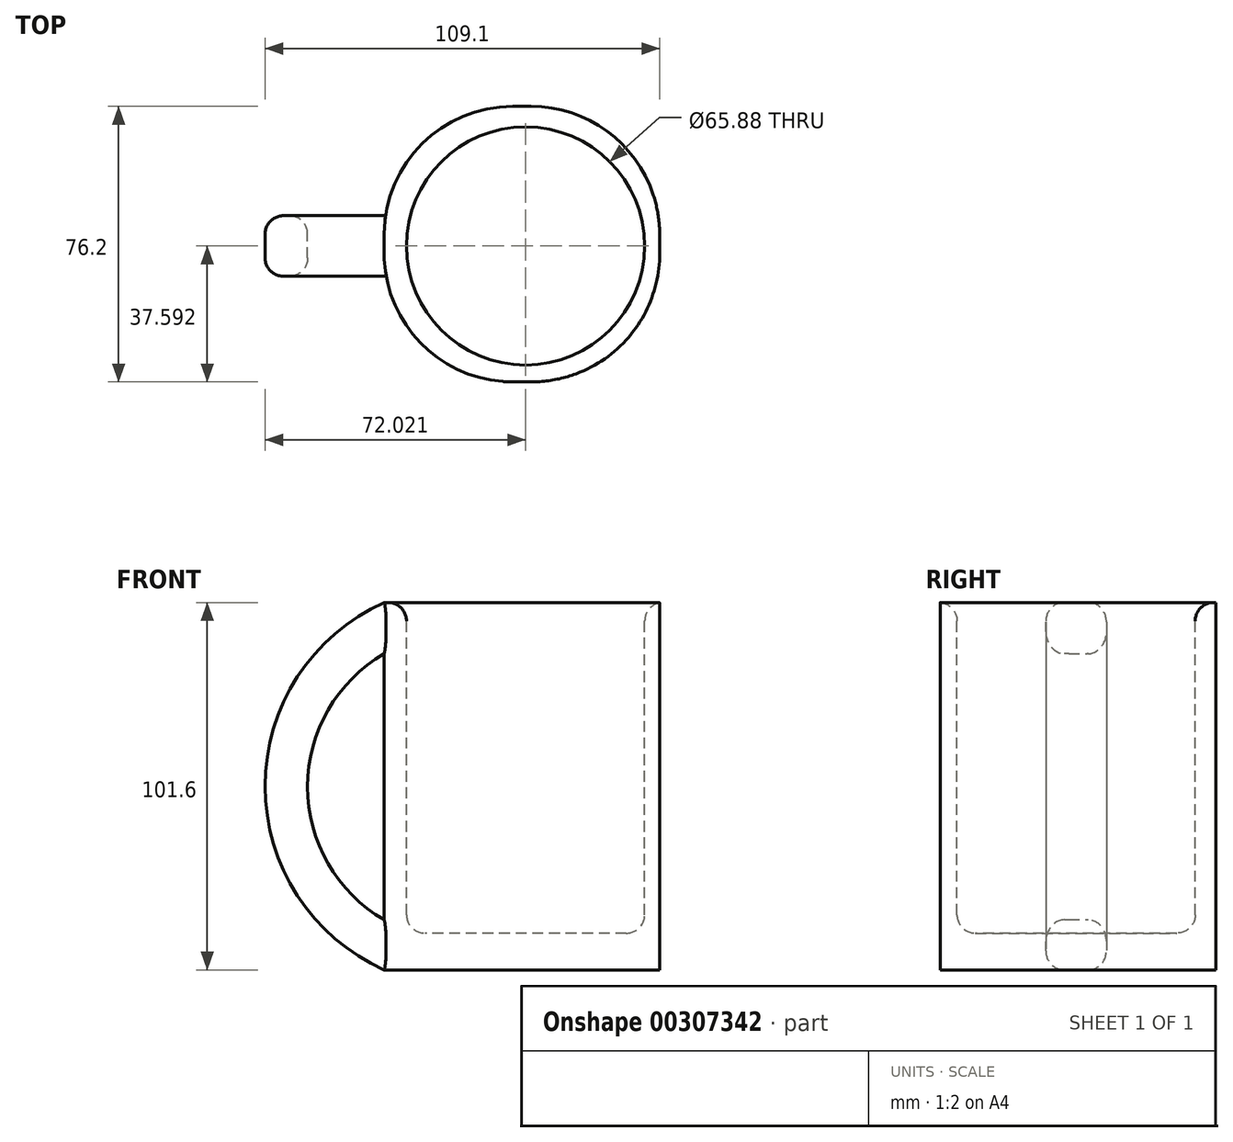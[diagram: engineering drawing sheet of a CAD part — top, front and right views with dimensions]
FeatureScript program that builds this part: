
annotation { "Feature Type Name" : "Feature", "Feature Type Description" : "" }
export const myFeature = defineFeature(function(context is Context, id is Id, definition is map)
    precondition{}
    {
        {
            var Q0;
            Q0=qCreatedBy(makeId("Front.planeOp"),FACE);
            var sketch = newSketch(context, id + "F0", { "sketchPlane" : qUnion([Q0])});
            skLineSegment(sketch, "E0", {"start": v(-63.5, 44.64) * mm, "end": v(-63.5, -56.96) * mm});
            skLineSegment(sketch, "E1", {"start": v(-63.5, -56.96) * mm, "end": v(12.7, -56.96) * mm});
            skLineSegment(sketch, "E2", {"start": v(12.7, -56.96) * mm, "end": v(12.7, 44.64) * mm});
            skLineSegment(sketch, "E3", {"start": v(-63.5, 44.64) * mm, "end": v(12.7, 44.64) * mm});
            skLineSegment(sketch, "E4", {"start": v(12.7, 40.44) * mm, "end": v(12.7, 27.74) * mm});
            skLineSegment(sketch, "E5", {"start": v(12.7, -37.39) * mm, "end": v(12.7, -50.09) * mm});
            skArc(sketch, "E6", {"start": v(-63.5, 44.64) * mm, "mid": v(-96.4, -6.16) * mm, "end": v(-63.5, -56.96) * mm});
            skArc(sketch, "E7", {"start": v(-63.5, 30.48) * mm, "mid": v(-84.66, -6.3) * mm, "end": v(-63.5, -43.09) * mm});
            skSolve(sketch);
        }
        {
            var Q0;
            {var subQ0=sQuery(id+"F0.wireOp",EDGE,"E1");Q0=makeQuery(id+"F0.imprint","IMPRINT",FACE,{"disambiguationData":[TD([[makeQuery(id+"F0.imprint","IMPRINT",EDGE,{"derivedFrom":subQ0}),1.0]])]});}
            extrude(context, id + "F1", {"entities" : qUnion([Q0]), "depth" : 76.2 * mm});
        }
        {
            var Q0;
            {var subQ0=sQuery(id+"F0.wireOp",EDGE,"E6");Q0=makeQuery(id+"F0.imprint","IMPRINT",FACE,{"disambiguationData":[TD([[makeQuery(id+"F0.imprint","IMPRINT",EDGE,{"derivedFrom":subQ0}),1.0]])]});}
            extrude(context, id + "F2", {"entities" : qUnion([Q0]), "operationType" : NewBodyOperationType.ADD, "depth" : 47 * mm, "hasSecondDirection" : true, "secondDirectionOppositeDirection" : false, "secondDirectionDepth" : 30.23 * mm});
        }
        {
            var Q0;
            Q0=makeQuery(id+"F1.opExtrude","SWEPT_FACE",FACE,{"disambiguationData":[OSD([sQuery(id+"F0.wireOp",EDGE,"E3")])]});
            var sketch = newSketch(context, id + "F3", { "sketchPlane" : qUnion([Q0])});
            skPoint(sketch, "E8.centerSnap0", {"position": v(-63.5, -38.6) * mm});
            skPoint(sketch, "E8.center.orphan", {"position": v(-29.14, -38.6) * mm});
            skCircle(sketch, "E9", {"center": v(-24.38, -38.6) * mm, "radius": 32.94 * mm});
            skSolve(sketch);
        }
        {
            var Q0;
            Q0=makeQuery(id+"F3.imprint","IMPRINT",FACE,{"disambiguationData":[TD([[makeQuery(id+"F3.imprint","IMPRINT",EDGE,{"derivedFrom":sQuery(id+"F3.wireOp",EDGE,"E9")}),1.0]])]});
            extrude(context, id + "F4", {"entities" : qUnion([Q0]), "operationType" : NewBodyOperationType.REMOVE, "oppositeDirection" : true, "depth" : 91.44 * mm});
        }
        {
            var Q0;
            Q0=makeQuery(id+"F1.opExtrude","CAP_EDGE",EDGE,{"disambiguationData":[OSD([sQuery(id+"F0.wireOp",EDGE,"E2"),sQuery(id+"F0.wireOp",EDGE,"E4"),sQuery(id+"F0.wireOp",EDGE,"E5")])],"isStart":false});
            var Q1;
            Q1=makeQuery(id+"F1.opExtrude","CAP_EDGE",EDGE,{"disambiguationData":[OSD([sQuery(id+"F0.wireOp",EDGE,"E0")])],"isStart":false});
            var Q2;
            Q2=makeQuery(id+"F1.opExtrude","CAP_EDGE",EDGE,{"disambiguationData":[OSD([sQuery(id+"F0.wireOp",EDGE,"E0")])],"isStart":true});
            var Q3;
            Q3=makeQuery(id+"F1.opExtrude","CAP_EDGE",EDGE,{"disambiguationData":[OSD([sQuery(id+"F0.wireOp",EDGE,"E2"),sQuery(id+"F0.wireOp",EDGE,"E4"),sQuery(id+"F0.wireOp",EDGE,"E5")])],"isStart":true});
            fillet(context, id + "F5", {"entities" : qUnion([Q0, Q1, Q2, Q3]), "radius" : 35.56 * mm, "tangentPropagation" : true, "allowEdgeOverflow" : false});
        }
        {
            var Q0;
            Q0=makeQuery(id+"F4.boolean.opBoolean","COPY",FACE,{"derivedFrom":makeQuery(id+"F4.opExtrude","SWEPT_FACE",FACE,{"disambiguationData":[OSD([sQuery(id+"F3.wireOp",EDGE,"E9")])]})});
            fillet(context, id + "F6", {"entities" : qUnion([Q0]), "radius" : 5.08 * mm, "tangentPropagation" : true, "allowEdgeOverflow" : false});
        }
        {
            var Q0;
            Q0=makeQuery(id+"F2.opExtrude","CAP_EDGE",EDGE,{"disambiguationData":[OSD([sQuery(id+"F0.wireOp",EDGE,"E6")])],"isStart":true});
            var Q1;
            Q1=makeQuery(id+"F2.opExtrude","CAP_EDGE",EDGE,{"disambiguationData":[OSD([sQuery(id+"F0.wireOp",EDGE,"E7")])],"isStart":true});
            var Q2;
            Q2=makeQuery(id+"F2.opExtrude","CAP_EDGE",EDGE,{"disambiguationData":[OSD([sQuery(id+"F0.wireOp",EDGE,"E6")])],"isStart":false});
            var Q3;
            Q3=makeQuery(id+"F2.opExtrude","CAP_EDGE",EDGE,{"disambiguationData":[OSD([sQuery(id+"F0.wireOp",EDGE,"E7")])],"isStart":false});
            fillet(context, id + "F7", {"entities" : qUnion([Q0, Q1, Q2, Q3]), "radius" : 5.08 * mm, "tangentPropagation" : true, "allowEdgeOverflow" : false});
        }
    });
